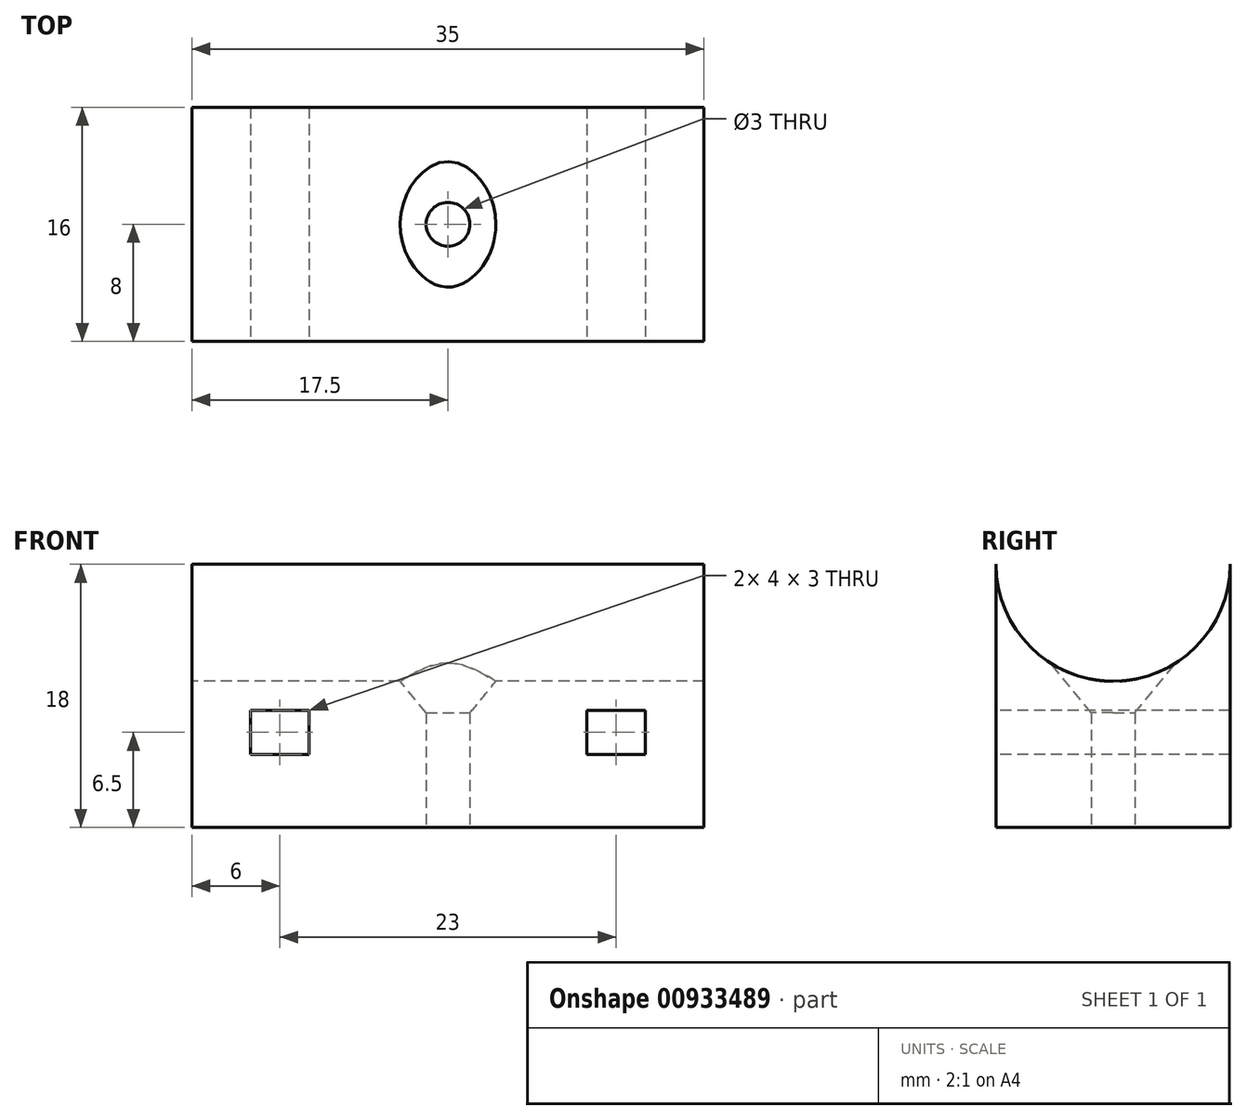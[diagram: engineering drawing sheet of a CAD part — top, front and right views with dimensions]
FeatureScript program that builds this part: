
annotation { "Feature Type Name" : "Feature", "Feature Type Description" : "" }
export const myFeature = defineFeature(function(context is Context, id is Id, definition is map)
    precondition{}
    {
        {
            var Q0;
            Q0=qCreatedBy(makeId("Top.planeOp"),FACE);
            var sketch = newSketch(context, id + "F0", { "sketchPlane" : qUnion([Q0])});
            skLineSegment(sketch, "E0.bottom", {"start": v(-17.5, 8) * mm, "end": v(17.5, 8) * mm});
            skLineSegment(sketch, "E0.top", {"start": v(-17.5, -8) * mm, "end": v(17.5, -8) * mm});
            skLineSegment(sketch, "E0.left", {"start": v(-17.5, 8) * mm, "end": v(-17.5, -8) * mm});
            skLineSegment(sketch, "E0.right", {"start": v(17.5, 8) * mm, "end": v(17.5, -8) * mm});
            skSolve(sketch);
        }
        {
            var Q0;
            Q0=makeQuery(id+"F0.imprint","IMPRINT",FACE,{"disambiguationData":[TD([[makeQuery(id+"F0.imprint","IMPRINT",EDGE,{"derivedFrom":sQuery(id+"F0.wireOp",EDGE,"E0.bottom")}),-1.0]])]});
            extrude(context, id + "F1", {"entities" : qUnion([Q0]), "depth" : 18 * mm, "offsetDistance" : 25 * mm});
        }
        {
            var Q0;
            Q0=makeQuery(id+"F1.opExtrude","SWEPT_FACE",FACE,{"disambiguationData":[OSD([sQuery(id+"F0.wireOp",EDGE,"E0.left")])]});
            var sketch = newSketch(context, id + "F2", { "sketchPlane" : qUnion([Q0])});
            skCircle(sketch, "E1", {"center": v(0, 18) * mm, "radius": 8 * mm});
            skSolve(sketch);
        }
        {
            var Q0;
            Q0 = qSketchRegion(id + "F2", true);
            extrude(context, id + "F3", {"entities" : qUnion([Q0]), "operationType" : NewBodyOperationType.REMOVE, "oppositeDirection" : true, "depth" : 40 * mm, "offsetDistance" : 25 * mm});
        }
        {
            var Q0;
            Q0=makeQuery(id+"F1.opExtrude","SWEPT_FACE",FACE,{"disambiguationData":[OSD([sQuery(id+"F0.wireOp",EDGE,"E0.top")])]});
            var sketch = newSketch(context, id + "F4", { "sketchPlane" : qUnion([Q0])});
            skLineSegment(sketch, "E2.bottom", {"start": v(-13.5, 8) * mm, "end": v(-9.5, 8) * mm});
            skLineSegment(sketch, "E2.top", {"start": v(-13.5, 5) * mm, "end": v(-9.5, 5) * mm});
            skLineSegment(sketch, "E2.left", {"start": v(-13.5, 8) * mm, "end": v(-13.5, 5) * mm});
            skLineSegment(sketch, "E2.right", {"start": v(-9.5, 8) * mm, "end": v(-9.5, 5) * mm});
            skLineSegment(sketch, "E3.bottom", {"start": v(9.5, 8) * mm, "end": v(13.5, 8) * mm});
            skLineSegment(sketch, "E3.top", {"start": v(9.5, 5) * mm, "end": v(13.5, 5) * mm});
            skLineSegment(sketch, "E3.left", {"start": v(9.5, 8) * mm, "end": v(9.5, 5) * mm});
            skLineSegment(sketch, "E3.right", {"start": v(13.5, 8) * mm, "end": v(13.5, 5) * mm});
            skSolve(sketch);
        }
        {
            var Q0;
            Q0 = qSketchRegion(id + "F4", true);
            extrude(context, id + "F5", {"entities" : qUnion([Q0]), "operationType" : NewBodyOperationType.REMOVE, "oppositeDirection" : true, "depth" : 25 * mm, "offsetDistance" : 25 * mm});
        }
        {
            var Q0;
            Q0=makeQuery(id+"F1.opExtrude","CAP_FACE",FACE,{"disambiguationData":[OSD([sQuery(id+"F0.wireOp",EDGE,"E0.bottom"),sQuery(id+"F0.wireOp",EDGE,"E0.top"),sQuery(id+"F0.wireOp",EDGE,"E0.left"),sQuery(id+"F0.wireOp",EDGE,"E0.right")])],"isStart":true});
            var sketch = newSketch(context, id + "F6", { "sketchPlane" : qUnion([Q0])});
            skCircle(sketch, "E4", {"center": v(0, 0) * mm, "radius": 1.5 * mm});
            skSolve(sketch);
        }
        {
            var Q0;
            Q0 = qSketchRegion(id + "F6", true);
            extrude(context, id + "F7", {"entities" : qUnion([Q0]), "operationType" : NewBodyOperationType.REMOVE, "endBound" : BoundingType.THROUGH_ALL, "oppositeDirection" : true, "depth" : 25 * mm, "offsetDistance" : 25 * mm});
        }
        {
            var Q0;
            Q0=qCreatedBy(makeId("Right.planeOp"),FACE);
            var sketch = newSketch(context, id + "F8", { "sketchPlane" : qUnion([Q0])});
            skLineSegment(sketch, "E5", {"start": v(0, 6) * mm, "end": v(-4.5, 11.5) * mm});
            skLineSegment(sketch, "E6", {"start": v(-4.5, 11.5) * mm, "end": v(0, 11.5) * mm});
            skLineSegment(sketch, "E7", {"start": v(0, 11.5) * mm, "end": v(0, 6) * mm});
            skSolve(sketch);
        }
        {
            var Q0;
            Q0 = qSketchRegion(id + "F8", true);
            var Q1;
            Q1=sQuery(id+"F8.wireOp",EDGE,"E7");
            revolve(context, id + "F9", {"operationType" : NewBodyOperationType.REMOVE, "surfaceOperationType" : NewSurfaceOperationType.NEW, "entities" : qUnion([Q0]), "axis" : qUnion([Q1]), "revolveType" : RevolveType.FULL, "oppositeDirection" : true});
        }
    });
